# Revit family: result
name_source: partatom
category: Plumbing Fixtures
revit_build: Autodesk Revit 2015 (Build: 20140903_1530(x64)
units: mm (PartAtom-declared; Revit-internal decimal feet)

## types (1)
- Default
    BIMobject category = Bath & Spas
    BIMobject category code = sanitary-bath-spas
    BIMobject main category = Sanitary
    BIMobject main category code = sanitary
    Brand url = http://www.duravit.com
    Edition number = 1
    GTIN code = https://4063382135650
    IFC Classification = Sanitary Terminal
    Manufacturer name = DURAVIT
    Masterformat 2014 Code = 13 17 33
    Masterformat 2014 Description = Whirlpool Tubs
    Material main = Acrylic
    NBS Reference Code = 35-06-08
    NBS Reference Description = Baths
    OmniClass Code = 23-31 15 00
    OmniClass Description = Bathtubs
    Product Guid = 2e9e30a0-d578-48fc-a4ed-1c91f8b2a8a3
    Product SKU = d-neo-whirltubs-760479
    Product data url = https://bimobject.com
    Product family = D-Neo
    Product group = Whirltubs
    Product name = 760479 D-Neo Whirltubs
    Product url = https://duravit-public-assets.s3.eu-central-1.amazonaws.com
    QR code = http://bimobject.com
    UNSPSC Code = 30181501
    Uniclass 1.4 Code = L72111
    Uniclass 1.4 Description = Spa baths, whirlpool baths
    Uniclass 2.0 Code = PR-35-06-08
    Uniclass 2.0 Description = Baths
    Uniclass 2015 Code = Pr_40_20_06_99
    Uniclass 2015 Name = Whirlpool baths
    Uniformat II Code = D2010
    Uniformat II Description = Plumbing Fixtures

## geometry (parser evidence)
native form markers: Sweep x4
no freeform markers — native parametric forms only
